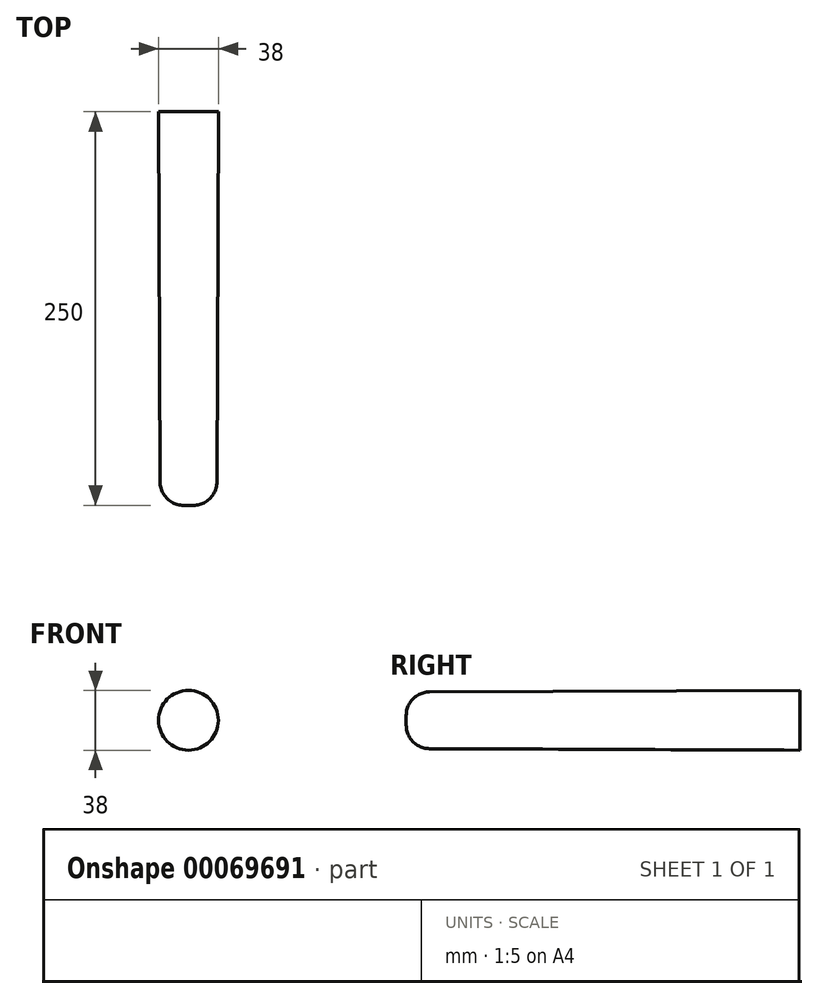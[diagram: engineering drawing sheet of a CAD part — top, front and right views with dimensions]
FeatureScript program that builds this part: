
annotation { "Feature Type Name" : "Feature", "Feature Type Description" : "" }
export const myFeature = defineFeature(function(context is Context, id is Id, definition is map)
    precondition{}
    {
        {
            var Q0;
            Q0=qCreatedBy(makeId("Front.planeOp"),FACE);
            var sketch = newSketch(context, id + "F0", { "sketchPlane" : qUnion([Q0])});
            skCircle(sketch, "E0", {"center": v(0, 0) * mm, "radius": 19 * mm});
            skSolve(sketch);
        }
        {
            var Q0;
            Q0=qCreatedBy(makeId("Front.planeOp"),FACE);
            cPlane(context, id + "F1", {"entities" : qUnion([Q0]), "cplaneType" : CPlaneType.OFFSET, "offset" : 250 * mm, "width" : 150 * mm, "height" : 150 * mm});
        }
        {
            var Q0;
            Q0=qCreatedBy(id+"F1.planeOp",FACE);
            var sketch = newSketch(context, id + "F2", { "sketchPlane" : qUnion([Q0])});
            skCircle(sketch, "E1", {"center": v(0, 0) * mm, "radius": 18 * mm});
            skSolve(sketch);
        }
        {
            var Q0;
            Q0=makeQuery(id+"F0.imprint","IMPRINT",FACE,{"disambiguationData":[TD([[makeQuery(id+"F0.imprint","IMPRINT",EDGE,{"derivedFrom":sQuery(id+"F0.wireOp",EDGE,"E0")}),1.0]])]});
            var Q1;
            Q1=makeQuery(id+"F2.imprint","IMPRINT",FACE,{"disambiguationData":[TD([[makeQuery(id+"F2.imprint","IMPRINT",EDGE,{"derivedFrom":sQuery(id+"F2.wireOp",EDGE,"E1")}),1.0]])]});
            loft(context, id + "F3", {"sheetProfilesArray" : [{ "sheetProfileEntities" : qUnion([Q0]) }, { "sheetProfileEntities" : qUnion([Q1]) }]});
        }
        {
            var Q0;
            Q0=makeQuery(id+"F3.opLoft","MID_CAP_EDGE",EDGE,{"disambiguationData":[OSD([sQuery(id+"F0.wireOp",EDGE,"E0"),sQuery(id+"F2.wireOp",EDGE,"E1")])],"capPos":1.0});
            fillet(context, id + "F4", {"entities" : qUnion([Q0]), "radius" : 15 * mm, "tangentPropagation" : true, "allowEdgeOverflow" : false});
        }
    });
